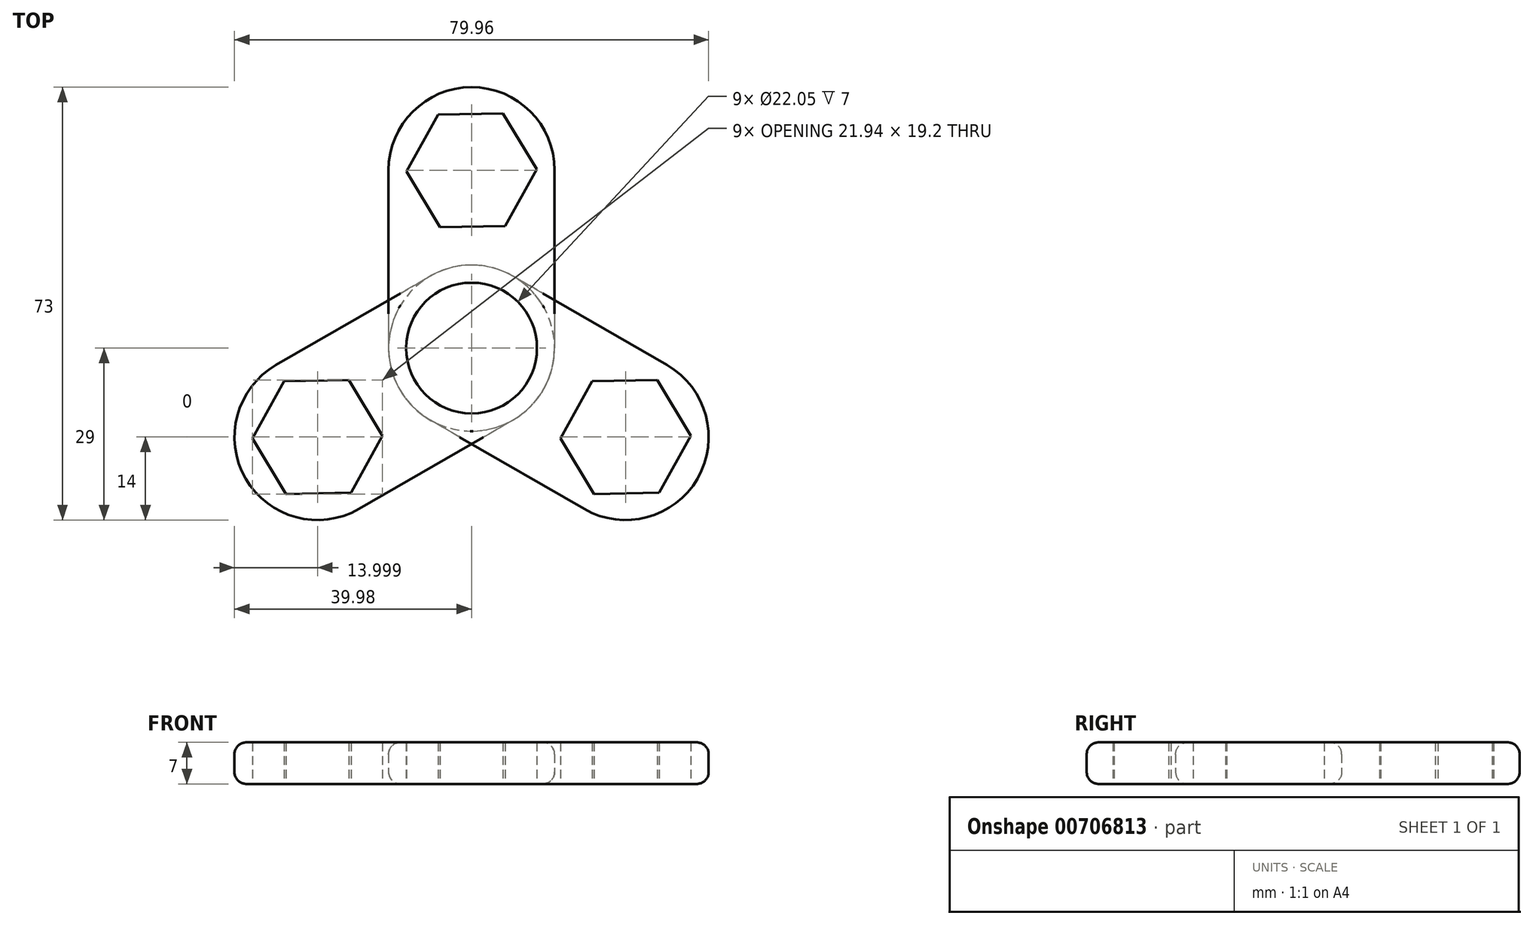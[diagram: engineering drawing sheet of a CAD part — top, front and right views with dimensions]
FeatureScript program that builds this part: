
annotation { "Feature Type Name" : "Feature", "Feature Type Description" : "" }
export const myFeature = defineFeature(function(context is Context, id is Id, definition is map)
    precondition{}
    {
        {
            var Q0;
            Q0=qCreatedBy(makeId("Top.planeOp"),FACE);
            var sketch = newSketch(context, id + "F0", { "sketchPlane" : qUnion([Q0])});
            skLineSegment(sketch, "E0.bottom", {"start": v(0, 0) * mm, "end": v(28, 0) * mm});
            skLineSegment(sketch, "E0.top", {"start": v(0, -30) * mm, "end": v(28, -30) * mm});
            skLineSegment(sketch, "E0.left", {"start": v(0, 0) * mm, "end": v(0, -30) * mm});
            skLineSegment(sketch, "E0.right", {"start": v(28, 0) * mm, "end": v(28, -30) * mm});
            skCircle(sketch, "E1", {"center": v(14, -30) * mm, "radius": 14 * mm});
            skCircle(sketch, "E2", {"center": v(14, -30) * mm, "radius": 11.03 * mm});
            skCircle(sketch, "E3.cCircle", {"center": v(14, 0) * mm, "radius": 9.5 * mm, "construction": true});
            skLineSegment(sketch, "E3.0", {"start": v(24.97, 0.2) * mm, "end": v(19.66, -9.4) * mm});
            skLineSegment(sketch, "E3.1", {"start": v(19.66, -9.4) * mm, "end": v(8.7, -9.6) * mm});
            skLineSegment(sketch, "E3.2", {"start": v(8.7, -9.6) * mm, "end": v(3.03, -0.2) * mm});
            skLineSegment(sketch, "E3.3", {"start": v(3.03, -0.2) * mm, "end": v(8.34, 9.4) * mm});
            skLineSegment(sketch, "E3.4", {"start": v(8.34, 9.4) * mm, "end": v(19.3, 9.6) * mm});
            skLineSegment(sketch, "E3.5", {"start": v(19.3, 9.6) * mm, "end": v(24.97, 0.2) * mm});
            skPoint(sketch, "E3.0.midPoint", {"position": v(22.31, -4.6) * mm});
            skCircle(sketch, "E4", {"center": v(14, 0) * mm, "radius": 14 * mm});
            skSolve(sketch);
        }
        {
            var Q0;
            {var subQ0=sQuery(id+"F0.wireOp",EDGE,"E3.4");Q0=makeQuery(id+"F0.imprint","IMPRINT",FACE,{"disambiguationData":[TD([[makeQuery(id+"F0.imprint","IMPRINT",EDGE,{"derivedFrom":subQ0}),1.0]])]});}
            var Q1;
            {var subQ0=sQuery(id+"F0.wireOp",EDGE,"E3.1");Q1=makeQuery(id+"F0.imprint","IMPRINT",FACE,{"disambiguationData":[TD([[makeQuery(id+"F0.imprint","IMPRINT",EDGE,{"derivedFrom":subQ0}),1.0]])]});}
            var Q2;
            {var subQ0=sQuery(id+"F0.wireOp",EDGE,"E0.left");Q2=makeQuery(id+"F0.imprint","IMPRINT",FACE,{"disambiguationData":[TD([[makeQuery(id+"F0.imprint","IMPRINT",EDGE,{"derivedFrom":subQ0}),1.0]])]});}
            var Q3;
            {var subQ1=sQuery(id+"F0.wireOp",EDGE,"E0.top");var subQ3=sQuery(id+"F0.wireOp",EDGE,"E2");var subQ4=makeQuery(id+"F0.imprint","INTERSECT",VERTEX,{"disambiguationData":[OD(0.0)],"derivedFrom":[subQ1,subQ3]});Q3=makeQuery(id+"F0.imprint","IMPRINT",FACE,{"disambiguationData":[TD([[makeQuery(id+"F0.imprint","IMPRINT",EDGE,{"disambiguationData":[TD([[subQ4,-1.0]])],"derivedFrom":subQ3}),-1.0]])]});}
            var Q4;
            {var subQ1=sQuery(id+"F0.wireOp",EDGE,"E0.top");var subQ3=sQuery(id+"F0.wireOp",EDGE,"E2");var subQ4=makeQuery(id+"F0.imprint","INTERSECT",VERTEX,{"disambiguationData":[OD(0.0)],"derivedFrom":[subQ1,subQ3]});Q4=makeQuery(id+"F0.imprint","IMPRINT",FACE,{"disambiguationData":[TD([[makeQuery(id+"F0.imprint","IMPRINT",EDGE,{"disambiguationData":[TD([[subQ4,1.0]])],"derivedFrom":subQ3}),-1.0]])]});}
            extrude(context, id + "F1", {"entities" : qUnion([Q0, Q1, Q2, Q3, Q4]), "depth" : 7 * mm, "offsetDistance" : 25 * mm});
        }
        {
            var Q0;
            Q0=makeQuery(id+"F1.opExtrude","CAP_EDGE",EDGE,{"disambiguationData":[OSD([sQuery(id+"F0.wireOp",EDGE,"E0.right")])],"isStart":false});
            var Q1;
            Q1=makeQuery(id+"F1.opExtrude","CAP_EDGE",EDGE,{"disambiguationData":[OSD([sQuery(id+"F0.wireOp",EDGE,"E4")])],"isStart":false});
            var Q2;
            Q2=makeQuery(id+"F1.opExtrude","CAP_EDGE",EDGE,{"disambiguationData":[OSD([sQuery(id+"F0.wireOp",EDGE,"E0.left")])],"isStart":true});
            var Q3;
            {var subQ0=sQuery(id+"F0.wireOp",EDGE,"E1");var subQ1=sQuery(id+"F0.wireOp",EDGE,"E0.top");Q3=makeQuery(id+"F1.opExtrude","CAP_EDGE",EDGE,{"disambiguationData":[OSD([subQ0]),TDD([makeQuery(id+"F0.imprint","IMPRINT",EDGE,{"disambiguationData":[TD([[makeQuery(id+"F0.imprint","INTERSECT",VERTEX,{"derivedFrom":[subQ1,sQuery(id+"F0.wireOp",EDGE,"E0.left"),subQ0]}),-1.0]])],"derivedFrom":subQ0})])],"isStart":true});}
            var Q4;
            Q4=makeQuery(id+"F1.opExtrude","CAP_EDGE",EDGE,{"disambiguationData":[OSD([sQuery(id+"F0.wireOp",EDGE,"E0.left")])],"isStart":false});
            var Q5;
            {var subQ0=sQuery(id+"F0.wireOp",EDGE,"E1");var subQ1=sQuery(id+"F0.wireOp",EDGE,"E0.top");Q5=makeQuery(id+"F1.opExtrude","CAP_EDGE",EDGE,{"disambiguationData":[OSD([subQ0]),TDD([makeQuery(id+"F0.imprint","IMPRINT",EDGE,{"disambiguationData":[TD([[makeQuery(id+"F0.imprint","INTERSECT",VERTEX,{"derivedFrom":[subQ1,sQuery(id+"F0.wireOp",EDGE,"E0.left"),subQ0]}),-1.0]])],"derivedFrom":subQ0})])],"isStart":false});}
            var Q6;
            Q6=makeQuery(id+"F1.opExtrude","CAP_EDGE",EDGE,{"disambiguationData":[OSD([sQuery(id+"F0.wireOp",EDGE,"E4")])],"isStart":true});
            var Q7;
            Q7=makeQuery(id+"F1.opExtrude","CAP_EDGE",EDGE,{"disambiguationData":[OSD([sQuery(id+"F0.wireOp",EDGE,"E0.right")])],"isStart":true});
            fillet(context, id + "F2", {"entities" : qUnion([Q0, Q1, Q2, Q3, Q4, Q5, Q6, Q7]), "radius" : 2 * mm, "tangentPropagation" : true, "allowEdgeOverflow" : false});
        }
        {
            var Q0;
            Q0=makeQuery(id+"F1.opExtrude","SWEPT_BODY",BODY,{"disambiguationData":[OSD([sQuery(id+"F0.wireOp",EDGE,"E0.left"),sQuery(id+"F0.wireOp",EDGE,"E0.right"),sQuery(id+"F0.wireOp",EDGE,"E1"),sQuery(id+"F0.wireOp",EDGE,"E2"),sQuery(id+"F0.wireOp",EDGE,"E3.0"),sQuery(id+"F0.wireOp",EDGE,"E3.1"),sQuery(id+"F0.wireOp",EDGE,"E3.2"),sQuery(id+"F0.wireOp",EDGE,"E3.3"),sQuery(id+"F0.wireOp",EDGE,"E3.4"),sQuery(id+"F0.wireOp",EDGE,"E3.5"),sQuery(id+"F0.wireOp",EDGE,"E4")])]});
            var Q1;
            Q1=makeQuery(id+"F1.opExtrude","CAP_EDGE",EDGE,{"disambiguationData":[OSD([sQuery(id+"F0.wireOp",EDGE,"E2")])],"isStart":false});
            circularPattern(context, id + "F3", {"entities" : qUnion([Q0]), "axis" : qUnion([Q1]), "angle" : 360 * degree, "instanceCount" : 3, "equalSpace" : true});
        }
    });
